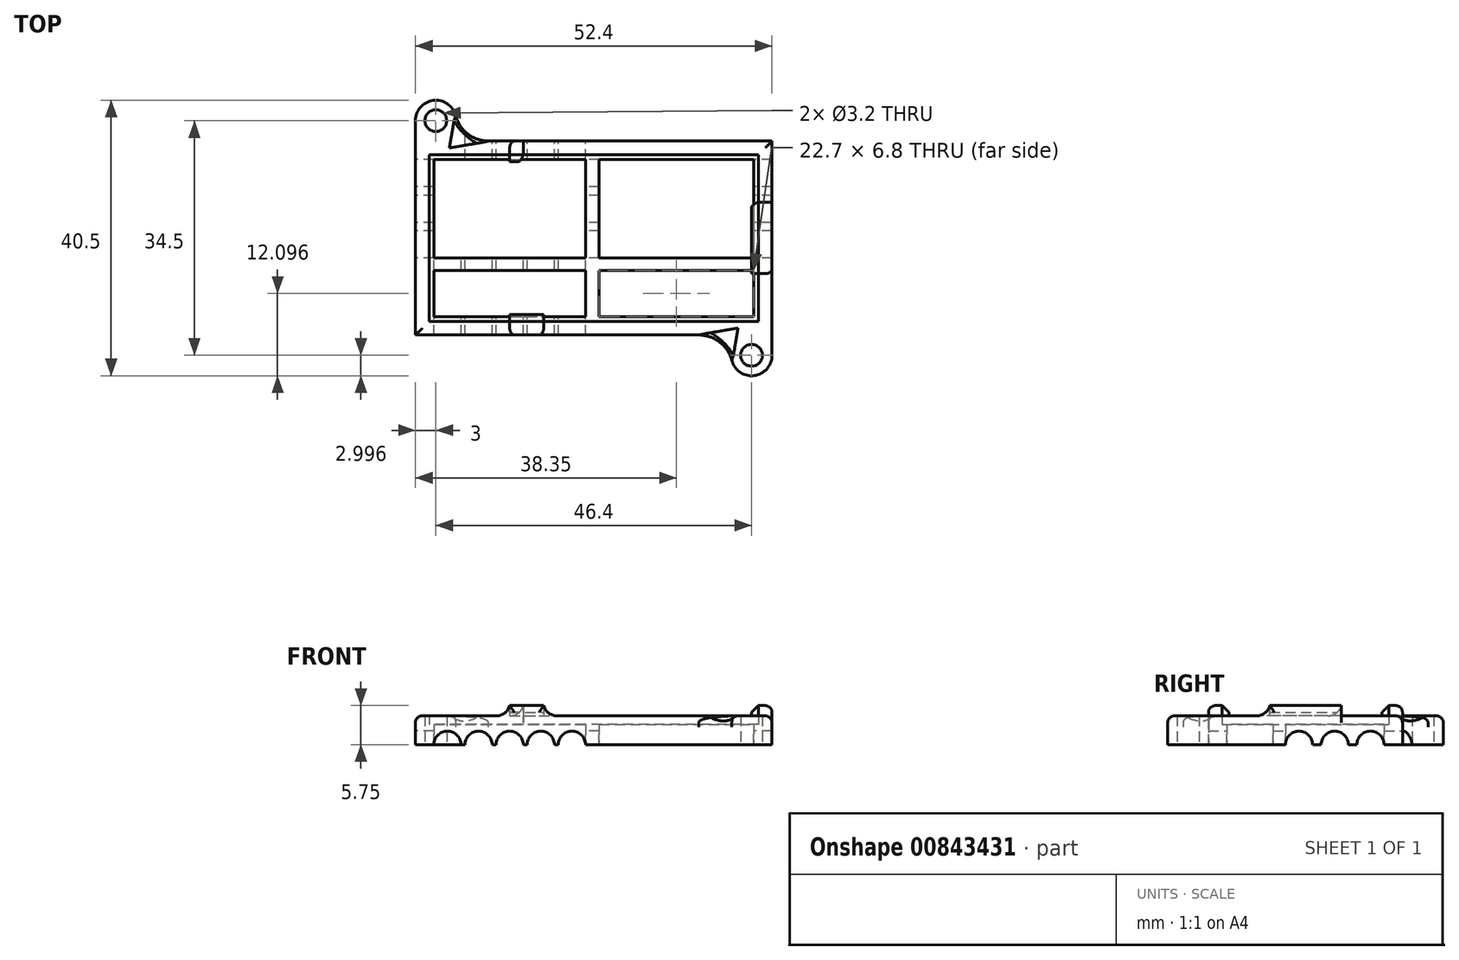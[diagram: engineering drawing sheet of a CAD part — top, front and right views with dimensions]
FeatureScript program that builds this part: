
annotation { "Feature Type Name" : "Feature", "Feature Type Description" : "" }
export const myFeature = defineFeature(function(context is Context, id is Id, definition is map)
    precondition{}
    {
        {
            var Q0;
            Q0=qCreatedBy(makeId("Top.planeOp"),FACE);
            var sketch = newSketch(context, id + "F0", { "sketchPlane" : qUnion([Q0])});
            skLineSegment(sketch, "E0.bottom", {"start": v(-17.25, 8.59) * mm, "end": v(31.15, 8.59) * mm});
            skLineSegment(sketch, "E0.top", {"start": v(-17.25, -15.91) * mm, "end": v(31.15, -15.91) * mm});
            skLineSegment(sketch, "E0.left", {"start": v(-17.25, 8.59) * mm, "end": v(-17.25, -15.91) * mm});
            skLineSegment(sketch, "E0.right", {"start": v(31.15, 8.59) * mm, "end": v(31.15, -15.91) * mm});
            skLineSegment(sketch, "E1.bottom", {"start": v(-19.25, 10.59) * mm, "end": v(33.15, 10.59) * mm});
            skLineSegment(sketch, "E1.top", {"start": v(-19.25, -17.91) * mm, "end": v(33.15, -17.91) * mm});
            skLineSegment(sketch, "E1.left", {"start": v(-19.25, 10.59) * mm, "end": v(-19.25, -17.91) * mm});
            skLineSegment(sketch, "E1.right", {"start": v(33.15, 10.59) * mm, "end": v(33.15, -17.91) * mm});
            skLineSegment(sketch, "E2.bottom", {"start": v(-16.55, 7.89) * mm, "end": v(5.75, 7.89) * mm});
            skLineSegment(sketch, "E2.top", {"start": v(-16.55, -15.21) * mm, "end": v(5.75, -15.21) * mm});
            skLineSegment(sketch, "E2.left", {"start": v(-16.55, 7.89) * mm, "end": v(-16.55, -6.61) * mm});
            skLineSegment(sketch, "E2.right", {"start": v(30.45, 7.89) * mm, "end": v(30.45, -6.61) * mm});
            skLineSegment(sketch, "E3", {"start": v(-16.55, -6.61) * mm, "end": v(5.75, -6.61) * mm});
            skLineSegment(sketch, "E4", {"start": v(-16.55, -8.41) * mm, "end": v(5.75, -8.41) * mm});
            skLineSegment(sketch, "E5", {"start": v(5.75, 7.89) * mm, "end": v(5.75, -6.61) * mm});
            skLineSegment(sketch, "E6", {"start": v(7.75, 7.89) * mm, "end": v(7.75, -6.61) * mm});
            skLineSegment(sketch, "E7.trimOffspring", {"start": v(7.75, -6.61) * mm, "end": v(30.45, -6.61) * mm});
            skLineSegment(sketch, "E8.trimOffspring", {"start": v(5.75, -8.41) * mm, "end": v(5.75, -15.21) * mm});
            skLineSegment(sketch, "E9.trimOffspring", {"start": v(7.75, -8.41) * mm, "end": v(7.75, -15.21) * mm});
            skLineSegment(sketch, "E10.trimOffspring", {"start": v(7.75, -8.41) * mm, "end": v(30.45, -8.41) * mm});
            skLineSegment(sketch, "E11.trimOffspring", {"start": v(-16.55, -8.41) * mm, "end": v(-16.55, -15.21) * mm});
            skLineSegment(sketch, "E12.trimOffspring", {"start": v(7.75, 7.89) * mm, "end": v(30.45, 7.89) * mm});
            skLineSegment(sketch, "E13.trimOffspring", {"start": v(30.45, -8.41) * mm, "end": v(30.45, -15.21) * mm});
            skLineSegment(sketch, "E14.trimOffspring", {"start": v(7.75, -15.21) * mm, "end": v(30.45, -15.21) * mm});
            skArc(sketch, "E15", {"start": v(-13.25, 13.59) * mm, "mid": v(-16.25, 16.59) * mm, "end": v(-19.25, 13.59) * mm});
            skLineSegment(sketch, "E16", {"start": v(-19.25, 13.59) * mm, "end": v(-19.25, 10.59) * mm});
            skLineSegment(sketch, "E17", {"start": v(-13.25, 13.59) * mm, "end": v(-13.25, 10.59) * mm});
            skArc(sketch, "E18", {"start": v(27.15, -20.91) * mm, "mid": v(30.15, -23.91) * mm, "end": v(33.15, -20.91) * mm});
            skLineSegment(sketch, "E19", {"start": v(33.15, -20.91) * mm, "end": v(33.15, -17.91) * mm});
            skLineSegment(sketch, "E20", {"start": v(27.15, -20.91) * mm, "end": v(27.15, -17.91) * mm});
            skSolve(sketch);
        }
        {
            var Q0;
            Q0 = qSketchRegion(id + "F0", true);
            var Q1;
            Q1=makeQuery(id+"F0.imprint","IMPRINT",FACE,{"disambiguationData":[TD([[makeQuery(id+"F0.imprint","IMPRINT",EDGE,{"derivedFrom":sQuery(id+"F0.wireOp",EDGE,"E0.bottom")}),-1.0]])]});
            extrude(context, id + "F1", {"entities" : qUnion([Q0, Q1]), "depth" : 3 * mm, "offsetDistance" : 25 * mm});
        }
        {
            var Q0;
            Q0=makeQuery(id+"F0.imprint","IMPRINT",FACE,{"disambiguationData":[TD([[makeQuery(id+"F0.imprint","IMPRINT",EDGE,{"derivedFrom":sQuery(id+"F0.wireOp",EDGE,"E0.bottom")}),1.0]])]});
            var Q1;
            Q1=makeQuery(id+"F0.imprint","IMPRINT",FACE,{"disambiguationData":[TD([[makeQuery(id+"F0.imprint","IMPRINT",EDGE,{"derivedFrom":sQuery(id+"F0.wireOp",EDGE,"E15")}),1.0]])]});
            var Q2;
            Q2=makeQuery(id+"F0.imprint","IMPRINT",FACE,{"disambiguationData":[TD([[makeQuery(id+"F0.imprint","IMPRINT",EDGE,{"derivedFrom":sQuery(id+"F0.wireOp",EDGE,"E18")}),1.0]])]});
            extrude(context, id + "F2", {"entities" : qUnion([Q0, Q1, Q2]), "operationType" : NewBodyOperationType.ADD, "depth" : 4.25 * mm, "offsetDistance" : 25 * mm});
        }
        {
            var Q0;
            Q0=sQuery(id+"F0.wireOp",VERTEX,"E15.center");
            var Q1;
            Q1=sQuery(id+"F0.wireOp",VERTEX,"E18.center");
            var Q2;
            Q2=makeQuery(id+"F1.opExtrude","SWEPT_BODY",BODY,{"disambiguationData":[OSD([sQuery(id+"F0.wireOp",EDGE,"E1.bottom"),sQuery(id+"F0.wireOp",EDGE,"E1.top"),sQuery(id+"F0.wireOp",EDGE,"E1.left"),sQuery(id+"F0.wireOp",EDGE,"E1.right"),sQuery(id+"F0.wireOp",EDGE,"E2.bottom"),sQuery(id+"F0.wireOp",EDGE,"E2.top"),sQuery(id+"F0.wireOp",EDGE,"E2.left"),sQuery(id+"F0.wireOp",EDGE,"E2.right"),sQuery(id+"F0.wireOp",EDGE,"E3"),sQuery(id+"F0.wireOp",EDGE,"E4"),sQuery(id+"F0.wireOp",EDGE,"E5"),sQuery(id+"F0.wireOp",EDGE,"E6"),sQuery(id+"F0.wireOp",EDGE,"E7.trimOffspring"),sQuery(id+"F0.wireOp",EDGE,"E8.trimOffspring"),sQuery(id+"F0.wireOp",EDGE,"E9.trimOffspring"),sQuery(id+"F0.wireOp",EDGE,"E10.trimOffspring"),sQuery(id+"F0.wireOp",EDGE,"E11.trimOffspring"),sQuery(id+"F0.wireOp",EDGE,"E12.trimOffspring"),sQuery(id+"F0.wireOp",EDGE,"E13.trimOffspring"),sQuery(id+"F0.wireOp",EDGE,"E14.trimOffspring"),sQuery(id+"F0.wireOp",EDGE,"E15"),sQuery(id+"F0.wireOp",EDGE,"E16"),sQuery(id+"F0.wireOp",EDGE,"E17"),sQuery(id+"F0.wireOp",EDGE,"E18"),sQuery(id+"F0.wireOp",EDGE,"E19"),sQuery(id+"F0.wireOp",EDGE,"E20")])]});
            hole(context, id + "F3", {"style" : HoleStyle.SIMPLE, "endStyle" : HoleEndStyle.BLIND, "oppositeDirection" : true, "holeDiameter" : 3.2 * mm, "majorDiameter" : 5 * mm, "holeDepth" : 4.5 * mm, "isTappedThrough" : true, "tappedDepth" : 12 * mm, "tapClearance" : 3, "startFromSketch" : true, "locations" : qUnion([Q0, Q1]), "scope" : qUnion([Q2])});
        }
        {
            var Q0;
            Q0=makeQuery(id+"F2.opExtrude","CAP_FACE",FACE,{"disambiguationData":[OSD([sQuery(id+"F0.wireOp",EDGE,"E0.bottom"),sQuery(id+"F0.wireOp",EDGE,"E0.top"),sQuery(id+"F0.wireOp",EDGE,"E0.left"),sQuery(id+"F0.wireOp",EDGE,"E0.right"),sQuery(id+"F0.wireOp",EDGE,"E1.bottom"),sQuery(id+"F0.wireOp",EDGE,"E1.top"),sQuery(id+"F0.wireOp",EDGE,"E1.left"),sQuery(id+"F0.wireOp",EDGE,"E1.right"),sQuery(id+"F0.wireOp",EDGE,"E15"),sQuery(id+"F0.wireOp",EDGE,"E16"),sQuery(id+"F0.wireOp",EDGE,"E17"),sQuery(id+"F0.wireOp",EDGE,"E18"),sQuery(id+"F0.wireOp",EDGE,"E19"),sQuery(id+"F0.wireOp",EDGE,"E20")])],"isStart":false});
            var sketch = newSketch(context, id + "F4", { "sketchPlane" : qUnion([Q0])});
            skLineSegment(sketch, "E21.bottom", {"start": v(-5.4, 10.59) * mm, "end": v(-3.4, 10.59) * mm});
            skLineSegment(sketch, "E21.top", {"start": v(-5.4, 7.59) * mm, "end": v(-3.4, 7.59) * mm});
            skLineSegment(sketch, "E21.left", {"start": v(-5.4, 10.59) * mm, "end": v(-5.4, 7.59) * mm});
            skLineSegment(sketch, "E21.right", {"start": v(-3.4, 10.59) * mm, "end": v(-3.4, 7.59) * mm});
            skLineSegment(sketch, "E22.bottom", {"start": v(-5.4, -17.91) * mm, "end": v(-0.4, -17.91) * mm});
            skLineSegment(sketch, "E22.top", {"start": v(-5.4, -14.91) * mm, "end": v(-0.4, -14.91) * mm});
            skLineSegment(sketch, "E22.left", {"start": v(-5.4, -17.91) * mm, "end": v(-5.4, -14.91) * mm});
            skLineSegment(sketch, "E22.right", {"start": v(-0.4, -17.91) * mm, "end": v(-0.4, -14.91) * mm});
            skLineSegment(sketch, "E23.bottom", {"start": v(33.15, 1.59) * mm, "end": v(30.15, 1.59) * mm});
            skLineSegment(sketch, "E23.top", {"start": v(33.15, -8.91) * mm, "end": v(30.15, -8.91) * mm});
            skLineSegment(sketch, "E23.left", {"start": v(33.15, 1.59) * mm, "end": v(33.15, -8.91) * mm});
            skLineSegment(sketch, "E23.right", {"start": v(30.15, 1.59) * mm, "end": v(30.15, -8.91) * mm});
            skSolve(sketch);
        }
        {
            var Q0;
            Q0 = qSketchRegion(id + "F4", true);
            extrude(context, id + "F5", {"entities" : qUnion([Q0]), "operationType" : NewBodyOperationType.ADD, "depth" : 1.5 * mm, "offsetDistance" : 25 * mm});
        }
        {
            var Q0;
            Q0=makeQuery(id+"F5.opExtrude","CAP_EDGE",EDGE,{"disambiguationData":[OSD([sQuery(id+"F4.wireOp",EDGE,"E21.top")])],"isStart":false});
            var Q1;
            Q1=makeQuery(id+"F5.opExtrude","CAP_EDGE",EDGE,{"disambiguationData":[OSD([sQuery(id+"F4.wireOp",EDGE,"E22.top")])],"isStart":false});
            var Q2;
            Q2=makeQuery(id+"F5.opExtrude","CAP_EDGE",EDGE,{"disambiguationData":[OSD([sQuery(id+"F4.wireOp",EDGE,"E23.right")])],"isStart":false});
            chamfer(context, id + "F6", {"entities" : qUnion([Q0, Q1, Q2]), "width" : 1 * mm, "tangentPropagation" : true});
        }
        {
            var Q0;
            {var subQ0=sQuery(id+"F4.wireOp",EDGE,"E21.right");Q0=makeQuery(id+"F5.boolean.opBoolean","SPLIT",EDGE,{"disambiguationData":[topologyDisambiguationEdgeConnected([makeQuery(id+"F2.opExtrude","CAP_FACE",FACE,{"disambiguationData":[OSD([sQuery(id+"F0.wireOp",EDGE,"E0.bottom"),sQuery(id+"F0.wireOp",EDGE,"E0.top"),sQuery(id+"F0.wireOp",EDGE,"E0.left"),sQuery(id+"F0.wireOp",EDGE,"E0.right"),sQuery(id+"F0.wireOp",EDGE,"E1.bottom"),sQuery(id+"F0.wireOp",EDGE,"E1.top"),sQuery(id+"F0.wireOp",EDGE,"E1.left"),sQuery(id+"F0.wireOp",EDGE,"E1.right"),sQuery(id+"F0.wireOp",EDGE,"E15"),sQuery(id+"F0.wireOp",EDGE,"E16"),sQuery(id+"F0.wireOp",EDGE,"E17"),sQuery(id+"F0.wireOp",EDGE,"E18"),sQuery(id+"F0.wireOp",EDGE,"E19"),sQuery(id+"F0.wireOp",EDGE,"E20")])],"isStart":false})])],"derivedFrom":makeQuery(id+"F5.opExtrude","CAP_EDGE",EDGE,{"disambiguationData":[OSD([subQ0])],"isStart":true})});}
            var Q1;
            {var subQ0=sQuery(id+"F4.wireOp",EDGE,"E21.left");Q1=makeQuery(id+"F5.boolean.opBoolean","SPLIT",EDGE,{"disambiguationData":[topologyDisambiguationEdgeConnected([makeQuery(id+"F2.opExtrude","CAP_FACE",FACE,{"disambiguationData":[OSD([sQuery(id+"F0.wireOp",EDGE,"E0.bottom"),sQuery(id+"F0.wireOp",EDGE,"E0.top"),sQuery(id+"F0.wireOp",EDGE,"E0.left"),sQuery(id+"F0.wireOp",EDGE,"E0.right"),sQuery(id+"F0.wireOp",EDGE,"E1.bottom"),sQuery(id+"F0.wireOp",EDGE,"E1.top"),sQuery(id+"F0.wireOp",EDGE,"E1.left"),sQuery(id+"F0.wireOp",EDGE,"E1.right"),sQuery(id+"F0.wireOp",EDGE,"E15"),sQuery(id+"F0.wireOp",EDGE,"E16"),sQuery(id+"F0.wireOp",EDGE,"E17"),sQuery(id+"F0.wireOp",EDGE,"E18"),sQuery(id+"F0.wireOp",EDGE,"E19"),sQuery(id+"F0.wireOp",EDGE,"E20")])],"isStart":false})])],"derivedFrom":makeQuery(id+"F5.opExtrude","CAP_EDGE",EDGE,{"disambiguationData":[OSD([subQ0])],"isStart":true})});}
            var Q2;
            {var subQ0=sQuery(id+"F4.wireOp",EDGE,"E22.right");Q2=makeQuery(id+"F5.boolean.opBoolean","SPLIT",EDGE,{"disambiguationData":[topologyDisambiguationEdgeConnected([makeQuery(id+"F2.opExtrude","CAP_FACE",FACE,{"disambiguationData":[OSD([sQuery(id+"F0.wireOp",EDGE,"E0.bottom"),sQuery(id+"F0.wireOp",EDGE,"E0.top"),sQuery(id+"F0.wireOp",EDGE,"E0.left"),sQuery(id+"F0.wireOp",EDGE,"E0.right"),sQuery(id+"F0.wireOp",EDGE,"E1.bottom"),sQuery(id+"F0.wireOp",EDGE,"E1.top"),sQuery(id+"F0.wireOp",EDGE,"E1.left"),sQuery(id+"F0.wireOp",EDGE,"E1.right"),sQuery(id+"F0.wireOp",EDGE,"E15"),sQuery(id+"F0.wireOp",EDGE,"E16"),sQuery(id+"F0.wireOp",EDGE,"E17"),sQuery(id+"F0.wireOp",EDGE,"E18"),sQuery(id+"F0.wireOp",EDGE,"E19"),sQuery(id+"F0.wireOp",EDGE,"E20")])],"isStart":false})])],"derivedFrom":makeQuery(id+"F5.opExtrude","CAP_EDGE",EDGE,{"disambiguationData":[OSD([subQ0])],"isStart":true})});}
            var Q3;
            {var subQ0=sQuery(id+"F4.wireOp",EDGE,"E22.left");Q3=makeQuery(id+"F5.boolean.opBoolean","SPLIT",EDGE,{"disambiguationData":[topologyDisambiguationEdgeConnected([makeQuery(id+"F2.opExtrude","CAP_FACE",FACE,{"disambiguationData":[OSD([sQuery(id+"F0.wireOp",EDGE,"E0.bottom"),sQuery(id+"F0.wireOp",EDGE,"E0.top"),sQuery(id+"F0.wireOp",EDGE,"E0.left"),sQuery(id+"F0.wireOp",EDGE,"E0.right"),sQuery(id+"F0.wireOp",EDGE,"E1.bottom"),sQuery(id+"F0.wireOp",EDGE,"E1.top"),sQuery(id+"F0.wireOp",EDGE,"E1.left"),sQuery(id+"F0.wireOp",EDGE,"E1.right"),sQuery(id+"F0.wireOp",EDGE,"E15"),sQuery(id+"F0.wireOp",EDGE,"E16"),sQuery(id+"F0.wireOp",EDGE,"E17"),sQuery(id+"F0.wireOp",EDGE,"E18"),sQuery(id+"F0.wireOp",EDGE,"E19"),sQuery(id+"F0.wireOp",EDGE,"E20")])],"isStart":false})])],"derivedFrom":makeQuery(id+"F5.opExtrude","CAP_EDGE",EDGE,{"disambiguationData":[OSD([subQ0])],"isStart":true})});}
            var Q4;
            {var subQ0=sQuery(id+"F4.wireOp",EDGE,"E23.top");Q4=makeQuery(id+"F5.boolean.opBoolean","SPLIT",EDGE,{"disambiguationData":[topologyDisambiguationEdgeConnected([makeQuery(id+"F2.opExtrude","CAP_FACE",FACE,{"disambiguationData":[OSD([sQuery(id+"F0.wireOp",EDGE,"E0.bottom"),sQuery(id+"F0.wireOp",EDGE,"E0.top"),sQuery(id+"F0.wireOp",EDGE,"E0.left"),sQuery(id+"F0.wireOp",EDGE,"E0.right"),sQuery(id+"F0.wireOp",EDGE,"E1.bottom"),sQuery(id+"F0.wireOp",EDGE,"E1.top"),sQuery(id+"F0.wireOp",EDGE,"E1.left"),sQuery(id+"F0.wireOp",EDGE,"E1.right"),sQuery(id+"F0.wireOp",EDGE,"E15"),sQuery(id+"F0.wireOp",EDGE,"E16"),sQuery(id+"F0.wireOp",EDGE,"E17"),sQuery(id+"F0.wireOp",EDGE,"E18"),sQuery(id+"F0.wireOp",EDGE,"E19"),sQuery(id+"F0.wireOp",EDGE,"E20")])],"isStart":false})])],"derivedFrom":makeQuery(id+"F5.opExtrude","CAP_EDGE",EDGE,{"disambiguationData":[OSD([subQ0])],"isStart":true})});}
            var Q5;
            {var subQ0=sQuery(id+"F4.wireOp",EDGE,"E23.bottom");Q5=makeQuery(id+"F5.boolean.opBoolean","SPLIT",EDGE,{"disambiguationData":[topologyDisambiguationEdgeConnected([makeQuery(id+"F2.opExtrude","CAP_FACE",FACE,{"disambiguationData":[OSD([sQuery(id+"F0.wireOp",EDGE,"E0.bottom"),sQuery(id+"F0.wireOp",EDGE,"E0.top"),sQuery(id+"F0.wireOp",EDGE,"E0.left"),sQuery(id+"F0.wireOp",EDGE,"E0.right"),sQuery(id+"F0.wireOp",EDGE,"E1.bottom"),sQuery(id+"F0.wireOp",EDGE,"E1.top"),sQuery(id+"F0.wireOp",EDGE,"E1.left"),sQuery(id+"F0.wireOp",EDGE,"E1.right"),sQuery(id+"F0.wireOp",EDGE,"E15"),sQuery(id+"F0.wireOp",EDGE,"E16"),sQuery(id+"F0.wireOp",EDGE,"E17"),sQuery(id+"F0.wireOp",EDGE,"E18"),sQuery(id+"F0.wireOp",EDGE,"E19"),sQuery(id+"F0.wireOp",EDGE,"E20")])],"isStart":false})])],"derivedFrom":makeQuery(id+"F5.opExtrude","CAP_EDGE",EDGE,{"disambiguationData":[OSD([subQ0])],"isStart":true})});}
            fillet(context, id + "F7", {"entities" : qUnion([Q0, Q1, Q2, Q3, Q4, Q5]), "radius" : 2 * mm, "tangentPropagation" : true, "allowEdgeOverflow" : false});
        }
        {
            var Q0;
            Q0=makeQuery(id+"F5.opExtrude","CAP_EDGE",EDGE,{"disambiguationData":[OSD([sQuery(id+"F4.wireOp",EDGE,"E21.bottom")])],"isStart":false});
            var Q1;
            Q1=makeQuery(id+"F5.opExtrude","CAP_EDGE",EDGE,{"disambiguationData":[OSD([sQuery(id+"F4.wireOp",EDGE,"E23.left")])],"isStart":false});
            var Q2;
            {var subQ0=sQuery(id+"F0.wireOp",EDGE,"E1.bottom");var subQ1=sQuery(id+"F0.wireOp",EDGE,"E19");var subQ2=sQuery(id+"F0.wireOp",EDGE,"E1.right");Q2=makeQuery(id+"F5.boolean.opBoolean","SPLIT",EDGE,{"disambiguationData":[TD([makeQuery(id+"F1.opExtrude","SWEPT_FACE",FACE,{"disambiguationData":[OSD([subQ0])]})])],"derivedFrom":makeQuery(id+"F2.opExtrude","CAP_EDGE",EDGE,{"disambiguationData":[OSD([subQ2,subQ1])],"isStart":false})});}
            var Q3;
            {var subQ0=sQuery(id+"F0.wireOp",EDGE,"E1.bottom");Q3=makeQuery(id+"F5.boolean.opBoolean","SPLIT",EDGE,{"disambiguationData":[TD([makeQuery(id+"F5.opExtrude","SWEPT_FACE",FACE,{"disambiguationData":[OSD([sQuery(id+"F4.wireOp",EDGE,"E21.right")])]})])],"derivedFrom":makeQuery(id+"F2.opExtrude","CAP_EDGE",EDGE,{"disambiguationData":[OSD([subQ0])],"isStart":false})});}
            var Q4;
            {var subQ0=sQuery(id+"F0.wireOp",EDGE,"E1.bottom");var subQ1=sQuery(id+"F0.wireOp",EDGE,"E17");Q4=makeQuery(id+"F5.boolean.opBoolean","SPLIT",EDGE,{"disambiguationData":[TD([makeQuery(id+"F1.opExtrude","SWEPT_FACE",FACE,{"disambiguationData":[OSD([subQ1])]})])],"derivedFrom":makeQuery(id+"F2.opExtrude","CAP_EDGE",EDGE,{"disambiguationData":[OSD([subQ0])],"isStart":false})});}
            var Q5;
            Q5=makeQuery(id+"F2.opExtrude","CAP_EDGE",EDGE,{"disambiguationData":[OSD([sQuery(id+"F0.wireOp",EDGE,"E17")])],"isStart":false});
            var Q6;
            {var subQ2=sQuery(id+"F0.wireOp",EDGE,"E1.top");Q6=makeQuery(id+"F5.boolean.opBoolean","SPLIT",EDGE,{"disambiguationData":[TD([makeQuery(id+"F5.opExtrude","SWEPT_FACE",FACE,{"disambiguationData":[OSD([sQuery(id+"F4.wireOp",EDGE,"E22.left")])]})])],"derivedFrom":makeQuery(id+"F2.opExtrude","CAP_EDGE",EDGE,{"disambiguationData":[OSD([subQ2])],"isStart":false})});}
            var Q7;
            Q7=makeQuery(id+"F5.opExtrude","CAP_EDGE",EDGE,{"disambiguationData":[OSD([sQuery(id+"F4.wireOp",EDGE,"E22.bottom")])],"isStart":false});
            var Q8;
            {var subQ0=sQuery(id+"F0.wireOp",EDGE,"E20");var subQ1=sQuery(id+"F0.wireOp",EDGE,"E1.top");Q8=makeQuery(id+"F5.boolean.opBoolean","SPLIT",EDGE,{"disambiguationData":[TD([makeQuery(id+"F1.opExtrude","SWEPT_FACE",FACE,{"disambiguationData":[OSD([subQ0])]})])],"derivedFrom":makeQuery(id+"F2.opExtrude","CAP_EDGE",EDGE,{"disambiguationData":[OSD([subQ1])],"isStart":false})});}
            var Q9;
            Q9=makeQuery(id+"F2.opExtrude","CAP_EDGE",EDGE,{"disambiguationData":[OSD([sQuery(id+"F0.wireOp",EDGE,"E18")])],"isStart":false});
            fillet(context, id + "F8", {"entities" : qUnion([Q0, Q1, Q2, Q3, Q4, Q5, Q6, Q7, Q8, Q9]), "radius" : 1 * mm, "tangentPropagation" : true, "allowEdgeOverflow" : false});
        }
        {
            var Q0;
            Q0=makeQuery(id+"F1.opExtrude","SWEPT_FACE",FACE,{"disambiguationData":[OSD([sQuery(id+"F0.wireOp",EDGE,"E5")])]});
            var sketch = newSketch(context, id + "F9", { "sketchPlane" : qUnion([Q0])});
            skCircle(sketch, "E24", {"center": v(-5.89, 0) * mm, "radius": 2 * mm});
            skCircle(sketch, "E25", {"center": v(4.61, 0) * mm, "radius": 2 * mm});
            skCircle(sketch, "E26", {"center": v(-0.64, 0) * mm, "radius": 2 * mm});
            skSolve(sketch);
        }
        {
            var Q0;
            Q0 = qSketchRegion(id + "F9", true);
            extrude(context, id + "F10", {"entities" : qUnion([Q0]), "operationType" : NewBodyOperationType.REMOVE, "endBound" : BoundingType.SYMMETRIC, "oppositeDirection" : true, "depth" : 102 * mm, "offsetDistance" : 25 * mm});
        }
        {
            var Q0;
            Q0=makeQuery(id+"F1.opExtrude","SWEPT_FACE",FACE,{"disambiguationData":[OSD([sQuery(id+"F0.wireOp",EDGE,"E3")])]});
            var sketch = newSketch(context, id + "F11", { "sketchPlane" : qUnion([Q0])});
            skCircle(sketch, "E27", {"center": v(-3.75, 0) * mm, "radius": 2 * mm});
            skCircle(sketch, "E28", {"center": v(14.55, 0) * mm, "radius": 2 * mm});
            skCircle(sketch, "E29", {"center": v(5.4, 0) * mm, "radius": 2 * mm});
            skCircle(sketch, "E30", {"center": v(9.98, 0) * mm, "radius": 2 * mm});
            skCircle(sketch, "E31", {"center": v(0.83, 0) * mm, "radius": 2 * mm});
            skSolve(sketch);
        }
        {
            var Q0;
            {var subQ0=sQuery(id+"F11.wireOp",EDGE,"E30");var subQ1=makeQuery(id+"F1.opExtrude","CAP_EDGE",EDGE,{"disambiguationData":[OSD([sQuery(id+"F0.wireOp",EDGE,"E3")])],"isStart":true});var subQ2=makeQuery(id+"F11.imprint","INTERSECT",VERTEX,{"disambiguationData":[OD(0.0)],"derivedFrom":[subQ1,subQ0]});Q0=makeQuery(id+"F11.imprint","IMPRINT",FACE,{"disambiguationData":[TD([[makeQuery(id+"F11.imprint","IMPRINT",EDGE,{"disambiguationData":[TD([[subQ2,-1.0]])],"derivedFrom":subQ0}),1.0]])]});}
            var Q1;
            {var subQ0=sQuery(id+"F11.wireOp",EDGE,"E29");var subQ1=makeQuery(id+"F1.opExtrude","CAP_EDGE",EDGE,{"disambiguationData":[OSD([sQuery(id+"F0.wireOp",EDGE,"E3")])],"isStart":true});var subQ2=makeQuery(id+"F11.imprint","INTERSECT",VERTEX,{"disambiguationData":[OD(0.0)],"derivedFrom":[subQ1,subQ0]});Q1=makeQuery(id+"F11.imprint","IMPRINT",FACE,{"disambiguationData":[TD([[makeQuery(id+"F11.imprint","IMPRINT",EDGE,{"disambiguationData":[TD([[subQ2,-1.0]])],"derivedFrom":subQ0}),1.0]])]});}
            var Q2;
            {var subQ0=sQuery(id+"F11.wireOp",EDGE,"E31");var subQ1=makeQuery(id+"F1.opExtrude","CAP_EDGE",EDGE,{"disambiguationData":[OSD([sQuery(id+"F0.wireOp",EDGE,"E3")])],"isStart":true});var subQ2=makeQuery(id+"F11.imprint","INTERSECT",VERTEX,{"disambiguationData":[OD(0.0)],"derivedFrom":[subQ1,subQ0]});Q2=makeQuery(id+"F11.imprint","IMPRINT",FACE,{"disambiguationData":[TD([[makeQuery(id+"F11.imprint","IMPRINT",EDGE,{"disambiguationData":[TD([[subQ2,1.0]])],"derivedFrom":subQ0}),1.0]])]});}
            var Q3;
            {var subQ0=sQuery(id+"F11.wireOp",EDGE,"E27");var subQ1=sQuery(id+"F0.wireOp",EDGE,"E3");var subQ2=makeQuery(id+"F1.opExtrude","CAP_EDGE",EDGE,{"disambiguationData":[OSD([subQ1])],"isStart":true});var subQ4=makeQuery(id+"F11.imprint","INTERSECT",VERTEX,{"derivedFrom":[subQ2,subQ0]});Q3=makeQuery(id+"F11.imprint","IMPRINT",FACE,{"disambiguationData":[TD([[makeQuery(id+"F11.imprint","IMPRINT",EDGE,{"disambiguationData":[TD([[subQ4,-1.0]])],"derivedFrom":subQ0}),1.0]])]});}
            extrude(context, id + "F12", {"entities" : qUnion([Q0, Q1, Q2, Q3]), "operationType" : NewBodyOperationType.REMOVE, "endBound" : BoundingType.SYMMETRIC, "oppositeDirection" : true, "depth" : 34.5 * mm, "offsetDistance" : 25 * mm});
        }
        {
            var Q0;
            {var subQ0=sQuery(id+"F11.wireOp",EDGE,"E28");var subQ1=sQuery(id+"F0.wireOp",EDGE,"E3");var subQ2=makeQuery(id+"F1.opExtrude","CAP_EDGE",EDGE,{"disambiguationData":[OSD([subQ1])],"isStart":true});var subQ4=makeQuery(id+"F11.imprint","INTERSECT",VERTEX,{"derivedFrom":[subQ2,subQ0]});Q0=makeQuery(id+"F11.imprint","IMPRINT",FACE,{"disambiguationData":[TD([[makeQuery(id+"F11.imprint","IMPRINT",EDGE,{"disambiguationData":[TD([[subQ4,1.0]])],"derivedFrom":subQ0}),1.0]])]});}
            extrude(context, id + "F13", {"entities" : qUnion([Q0]), "operationType" : NewBodyOperationType.REMOVE, "oppositeDirection" : true, "depth" : 25 * mm, "offsetDistance" : 25 * mm});
        }
        {
            var Q0;
            {var subQ0=sQuery(id+"F0.wireOp",EDGE,"E17");var subQ1=sQuery(id+"F0.wireOp",EDGE,"E1.bottom");Q0=makeQuery(id+"F2.boolean.opBoolean","MERGE",EDGE,{"derivedFrom":[makeQuery(id+"F1.opExtrude","SWEPT_EDGE",EDGE,{"disambiguationData":[OSD([subQ1,subQ0])]}),makeQuery(id+"F2.opExtrude","SWEPT_EDGE",EDGE,{"disambiguationData":[OSD([subQ1,subQ0])]})]});}
            var Q1;
            {var subQ0=sQuery(id+"F0.wireOp",EDGE,"E20");var subQ1=sQuery(id+"F0.wireOp",EDGE,"E1.top");Q1=makeQuery(id+"F2.boolean.opBoolean","MERGE",EDGE,{"derivedFrom":[makeQuery(id+"F1.opExtrude","SWEPT_EDGE",EDGE,{"disambiguationData":[OSD([subQ1,subQ0])]}),makeQuery(id+"F2.opExtrude","SWEPT_EDGE",EDGE,{"disambiguationData":[OSD([subQ1,subQ0])]})]});}
            fillet(context, id + "F14", {"entities" : qUnion([Q0, Q1]), "radius" : 5 * mm, "tangentPropagation" : true, "allowEdgeOverflow" : false});
        }
    });
